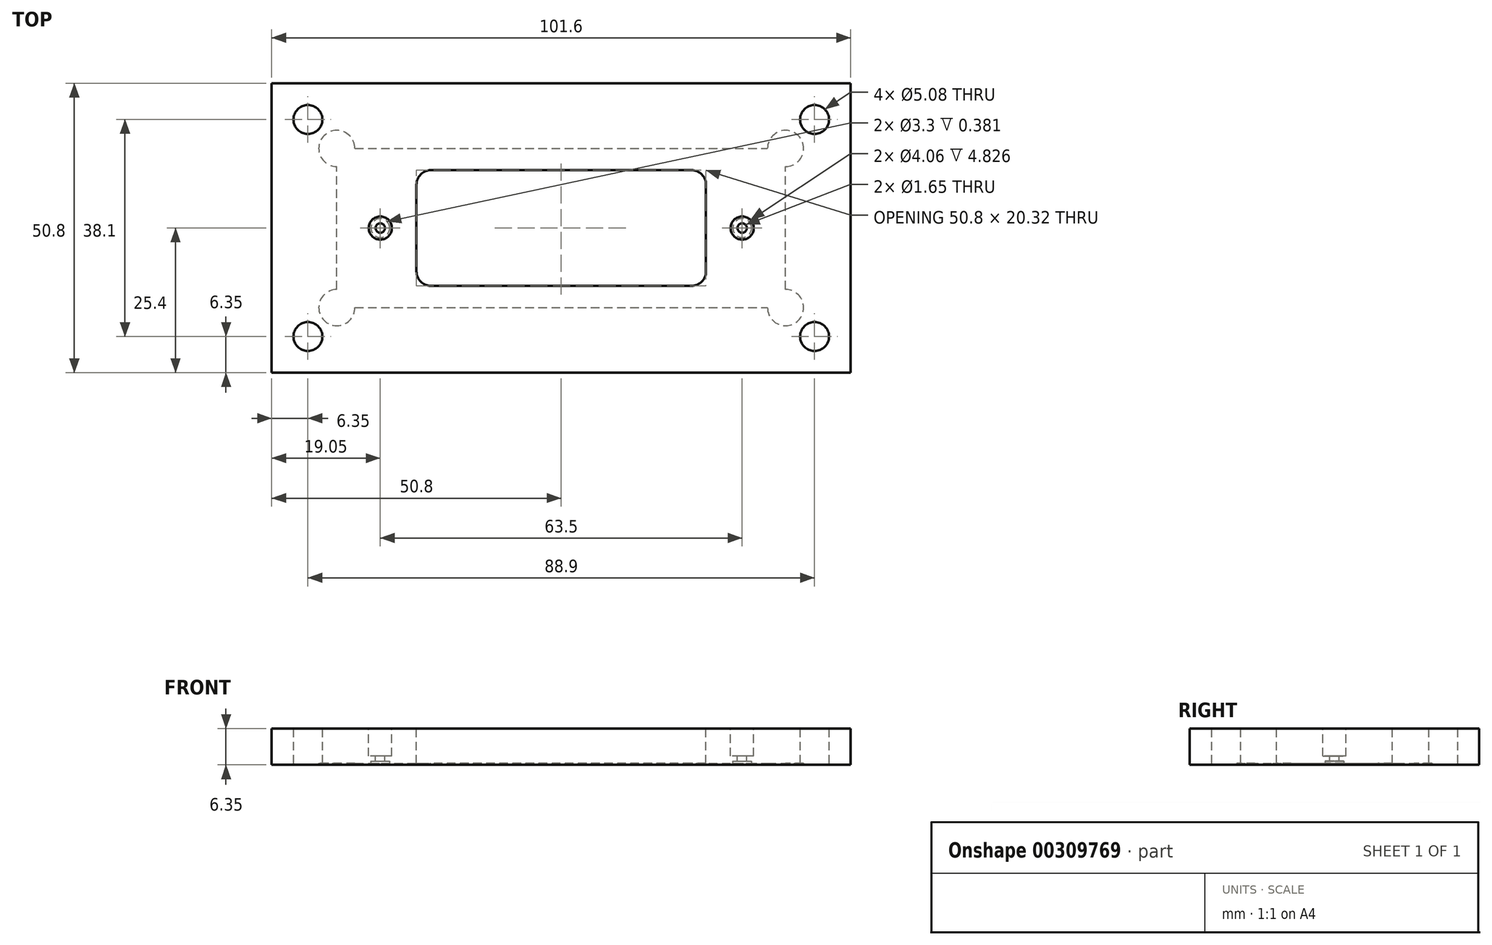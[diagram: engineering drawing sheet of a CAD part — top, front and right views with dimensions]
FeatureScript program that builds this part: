
annotation { "Feature Type Name" : "Feature", "Feature Type Description" : "" }
export const myFeature = defineFeature(function(context is Context, id is Id, definition is map)
    precondition{}
    {
        {
            var Q0;
            Q0=qCreatedBy(makeId("Top.planeOp"),FACE);
            var sketch = newSketch(context, id + "F0", { "sketchPlane" : qUnion([Q0])});
            skLineSegment(sketch, "E0.bottom", {"start": v(0, 0) * mm, "end": v(101.6, 0) * mm});
            skLineSegment(sketch, "E0.top", {"start": v(0, 50.8) * mm, "end": v(101.6, 50.8) * mm});
            skLineSegment(sketch, "E0.left", {"start": v(0, 0) * mm, "end": v(0, 50.8) * mm});
            skLineSegment(sketch, "E0.right", {"start": v(101.6, 0) * mm, "end": v(101.6, 50.8) * mm});
            skSolve(sketch);
        }
        {
            var Q0;
            Q0=makeQuery(id+"F0.imprint","IMPRINT",FACE,{"disambiguationData":[TD([[makeQuery(id+"F0.imprint","IMPRINT",EDGE,{"derivedFrom":sQuery(id+"F0.wireOp",EDGE,"E0.bottom")}),1.0]])]});
            extrude(context, id + "F1", {"entities" : qUnion([Q0]), "depth" : 6.35 * mm});
        }
        {
            var Q0;
            Q0=makeQuery(id+"F1.opExtrude","CAP_FACE",FACE,{"disambiguationData":[OSD([sQuery(id+"F0.wireOp",EDGE,"E0.bottom"),sQuery(id+"F0.wireOp",EDGE,"E0.top"),sQuery(id+"F0.wireOp",EDGE,"E0.left"),sQuery(id+"F0.wireOp",EDGE,"E0.right")])],"isStart":true});
            var sketch = newSketch(context, id + "F2", { "sketchPlane" : qUnion([Q0])});
            skLineSegment(sketch, "E1.bottom", {"start": v(11.43, -11.43) * mm, "end": v(90.17, -11.43) * mm});
            skLineSegment(sketch, "E1.top", {"start": v(11.43, -39.37) * mm, "end": v(90.17, -39.37) * mm});
            skLineSegment(sketch, "E1.left", {"start": v(11.43, -11.43) * mm, "end": v(11.43, -39.37) * mm});
            skLineSegment(sketch, "E1.right", {"start": v(90.17, -11.43) * mm, "end": v(90.17, -39.37) * mm});
            skCircle(sketch, "E2", {"center": v(11.43, -11.43) * mm, "radius": 3.18 * mm});
            skCircle(sketch, "E3", {"center": v(90.17, -11.43) * mm, "radius": 3.18 * mm});
            skCircle(sketch, "E4", {"center": v(90.17, -39.37) * mm, "radius": 3.18 * mm});
            skCircle(sketch, "E5", {"center": v(11.43, -39.37) * mm, "radius": 3.18 * mm});
            skSolve(sketch);
        }
        {
            var Q0;
            Q0 = qSketchRegion(id + "F2", true);
            extrude(context, id + "F3", {"entities" : qUnion([Q0]), "operationType" : NewBodyOperationType.REMOVE, "oppositeDirection" : true, "depth" : 0.25 * mm});
        }
        {
            var Q0;
            Q0=makeQuery(id+"F3.boolean.opBoolean","COPY",FACE,{"derivedFrom":makeQuery(id+"F3.opExtrude","CAP_FACE",FACE,{"disambiguationData":[OSD([sQuery(id+"F2.wireOp",EDGE,"E1.bottom"),sQuery(id+"F2.wireOp",EDGE,"E1.top"),sQuery(id+"F2.wireOp",EDGE,"E1.left"),sQuery(id+"F2.wireOp",EDGE,"E1.right"),sQuery(id+"F2.wireOp",EDGE,"E2"),sQuery(id+"F2.wireOp",EDGE,"E3"),sQuery(id+"F2.wireOp",EDGE,"E4"),sQuery(id+"F2.wireOp",EDGE,"E5")])],"isStart":false})});
            var sketch = newSketch(context, id + "F4", { "sketchPlane" : qUnion([Q0])});
            skLineSegment(sketch, "E6.bottom", {"start": v(27.94, -35.56) * mm, "end": v(73.66, -35.56) * mm});
            skLineSegment(sketch, "E6.top", {"start": v(27.94, -15.24) * mm, "end": v(73.66, -15.24) * mm});
            skLineSegment(sketch, "E6.left", {"start": v(25.4, -33.02) * mm, "end": v(25.4, -17.78) * mm});
            skLineSegment(sketch, "E6.right", {"start": v(76.2, -33.02) * mm, "end": v(76.2, -17.78) * mm});
            skPoint(sketch, "E7.visualSharp", {"position": v(25.4, -15.24) * mm});
            skArc(sketch, "E7.filletArc", {"start": v(27.94, -15.24) * mm, "mid": v(26.14, -15.98) * mm, "end": v(25.4, -17.78) * mm});
            skPoint(sketch, "E8.visualSharp", {"position": v(76.2, -15.24) * mm});
            skArc(sketch, "E8.filletArc", {"start": v(76.2, -17.78) * mm, "mid": v(75.46, -15.98) * mm, "end": v(73.66, -15.24) * mm});
            skPoint(sketch, "E9.visualSharp", {"position": v(76.2, -35.56) * mm});
            skArc(sketch, "E9.filletArc", {"start": v(73.66, -35.56) * mm, "mid": v(75.46, -34.82) * mm, "end": v(76.2, -33.02) * mm});
            skPoint(sketch, "E10.visualSharp", {"position": v(25.4, -35.56) * mm});
            skArc(sketch, "E10.filletArc", {"start": v(25.4, -33.02) * mm, "mid": v(26.14, -34.82) * mm, "end": v(27.94, -35.56) * mm});
            skSolve(sketch);
        }
        {
            var Q0;
            Q0=makeQuery(id+"F4.imprint","IMPRINT",FACE,{"disambiguationData":[TD([[makeQuery(id+"F4.imprint","IMPRINT",EDGE,{"derivedFrom":sQuery(id+"F4.wireOp",EDGE,"E6.bottom")}),1.0]])]});
            extrude(context, id + "F5", {"entities" : qUnion([Q0]), "operationType" : NewBodyOperationType.REMOVE, "depth" : 25.4 * mm, "hasSecondDirection" : true, "secondDirectionOppositeDirection" : true, "secondDirectionDepth" : 25.4 * mm});
        }
        {
            var Q0;
            Q0=makeQuery(id+"F3.boolean.opBoolean","COPY",FACE,{"derivedFrom":makeQuery(id+"F3.opExtrude","CAP_FACE",FACE,{"disambiguationData":[OSD([sQuery(id+"F2.wireOp",EDGE,"E1.bottom"),sQuery(id+"F2.wireOp",EDGE,"E1.top"),sQuery(id+"F2.wireOp",EDGE,"E1.left"),sQuery(id+"F2.wireOp",EDGE,"E1.right"),sQuery(id+"F2.wireOp",EDGE,"E2"),sQuery(id+"F2.wireOp",EDGE,"E3"),sQuery(id+"F2.wireOp",EDGE,"E4"),sQuery(id+"F2.wireOp",EDGE,"E5")])],"isStart":false})});
            var sketch = newSketch(context, id + "F6", { "sketchPlane" : qUnion([Q0])});
            skCircle(sketch, "E11", {"center": v(19.05, -25.4) * mm, "radius": 1.65 * mm});
            skCircle(sketch, "E12", {"center": v(82.55, -25.4) * mm, "radius": 1.65 * mm});
            skSolve(sketch);
        }
        {
            var Q0;
            Q0=makeQuery(id+"F6.imprint","IMPRINT",FACE,{"disambiguationData":[TD([[makeQuery(id+"F6.imprint","IMPRINT",EDGE,{"derivedFrom":sQuery(id+"F6.wireOp",EDGE,"E12")}),1.0]])]});
            var Q1;
            Q1=makeQuery(id+"F6.imprint","IMPRINT",FACE,{"disambiguationData":[TD([[makeQuery(id+"F6.imprint","IMPRINT",EDGE,{"derivedFrom":sQuery(id+"F6.wireOp",EDGE,"E11")}),1.0]])]});
            extrude(context, id + "F7", {"entities" : qUnion([Q0, Q1]), "operationType" : NewBodyOperationType.REMOVE, "oppositeDirection" : true, "depth" : 0.38 * mm});
        }
        {
            var Q0;
            Q0=makeQuery(id+"F1.opExtrude","CAP_FACE",FACE,{"disambiguationData":[OSD([sQuery(id+"F0.wireOp",EDGE,"E0.bottom"),sQuery(id+"F0.wireOp",EDGE,"E0.top"),sQuery(id+"F0.wireOp",EDGE,"E0.left"),sQuery(id+"F0.wireOp",EDGE,"E0.right")])],"isStart":false});
            var sketch = newSketch(context, id + "F8", { "sketchPlane" : qUnion([Q0])});
            skCircle(sketch, "E13", {"center": v(19.05, 25.4) * mm, "radius": 2.03 * mm});
            skCircle(sketch, "E14", {"center": v(82.55, 25.4) * mm, "radius": 2.03 * mm});
            skSolve(sketch);
        }
        {
            var Q0;
            Q0=makeQuery(id+"F8.imprint","IMPRINT",FACE,{"disambiguationData":[TD([[makeQuery(id+"F8.imprint","IMPRINT",EDGE,{"derivedFrom":sQuery(id+"F8.wireOp",EDGE,"E13")}),1.0]])]});
            var Q1;
            Q1=makeQuery(id+"F8.imprint","IMPRINT",FACE,{"disambiguationData":[TD([[makeQuery(id+"F8.imprint","IMPRINT",EDGE,{"derivedFrom":sQuery(id+"F8.wireOp",EDGE,"E14")}),1.0]])]});
            extrude(context, id + "F9", {"entities" : qUnion([Q0, Q1]), "operationType" : NewBodyOperationType.REMOVE, "oppositeDirection" : true, "depth" : 4.83 * mm});
        }
        {
            var Q0;
            Q0=makeQuery(id+"F7.boolean.opBoolean","COPY",FACE,{"derivedFrom":makeQuery(id+"F7.opExtrude","CAP_FACE",FACE,{"disambiguationData":[OSD([sQuery(id+"F6.wireOp",EDGE,"E12")])],"isStart":false})});
            var sketch = newSketch(context, id + "F10", { "sketchPlane" : qUnion([Q0])});
            skCircle(sketch, "E15", {"center": v(19.05, -25.4) * mm, "radius": 0.83 * mm});
            skCircle(sketch, "E16", {"center": v(82.55, -25.4) * mm, "radius": 0.83 * mm});
            skSolve(sketch);
        }
        {
            var Q0;
            Q0=makeQuery(id+"F10.imprint","IMPRINT",FACE,{"disambiguationData":[TD([[makeQuery(id+"F10.imprint","IMPRINT",EDGE,{"derivedFrom":sQuery(id+"F10.wireOp",EDGE,"E15")}),1.0]])]});
            var Q1;
            Q1=makeQuery(id+"F10.imprint","IMPRINT",FACE,{"disambiguationData":[TD([[makeQuery(id+"F10.imprint","IMPRINT",EDGE,{"derivedFrom":sQuery(id+"F10.wireOp",EDGE,"E16")}),1.0]])]});
            extrude(context, id + "F11", {"entities" : qUnion([Q0, Q1]), "operationType" : NewBodyOperationType.REMOVE, "depth" : 25.4 * mm, "hasSecondDirection" : true, "secondDirectionBound" : SecondDirectionBoundingType.THROUGH_ALL, "secondDirectionOppositeDirection" : true, "secondDirectionDepth" : 25.4 * mm});
        }
        {
            var Q0;
            Q0=makeQuery(id+"F1.opExtrude","CAP_FACE",FACE,{"disambiguationData":[OSD([sQuery(id+"F0.wireOp",EDGE,"E0.bottom"),sQuery(id+"F0.wireOp",EDGE,"E0.top"),sQuery(id+"F0.wireOp",EDGE,"E0.left"),sQuery(id+"F0.wireOp",EDGE,"E0.right")])],"isStart":true});
            var sketch = newSketch(context, id + "F12", { "sketchPlane" : qUnion([Q0])});
            skCircle(sketch, "E17", {"center": v(6.35, -6.35) * mm, "radius": 2.54 * mm});
            skCircle(sketch, "E18", {"center": v(95.25, -6.35) * mm, "radius": 2.54 * mm});
            skCircle(sketch, "E19", {"center": v(95.25, -44.45) * mm, "radius": 2.54 * mm});
            skCircle(sketch, "E20", {"center": v(6.35, -44.45) * mm, "radius": 2.54 * mm});
            skSolve(sketch);
        }
        {
            var Q0;
            Q0=makeQuery(id+"F12.imprint","IMPRINT",FACE,{"disambiguationData":[TD([[makeQuery(id+"F12.imprint","IMPRINT",EDGE,{"derivedFrom":sQuery(id+"F12.wireOp",EDGE,"E18")}),1.0]])]});
            var Q1;
            Q1=makeQuery(id+"F12.imprint","IMPRINT",FACE,{"disambiguationData":[TD([[makeQuery(id+"F12.imprint","IMPRINT",EDGE,{"derivedFrom":sQuery(id+"F12.wireOp",EDGE,"E17")}),1.0]])]});
            var Q2;
            Q2=makeQuery(id+"F12.imprint","IMPRINT",FACE,{"disambiguationData":[TD([[makeQuery(id+"F12.imprint","IMPRINT",EDGE,{"derivedFrom":sQuery(id+"F12.wireOp",EDGE,"E20")}),1.0]])]});
            var Q3;
            Q3=makeQuery(id+"F12.imprint","IMPRINT",FACE,{"disambiguationData":[TD([[makeQuery(id+"F12.imprint","IMPRINT",EDGE,{"derivedFrom":sQuery(id+"F12.wireOp",EDGE,"E19")}),1.0]])]});
            extrude(context, id + "F13", {"entities" : qUnion([Q0, Q1, Q2, Q3]), "operationType" : NewBodyOperationType.REMOVE, "endBound" : BoundingType.THROUGH_ALL, "oppositeDirection" : true, "depth" : 25.4 * mm});
        }
    });
